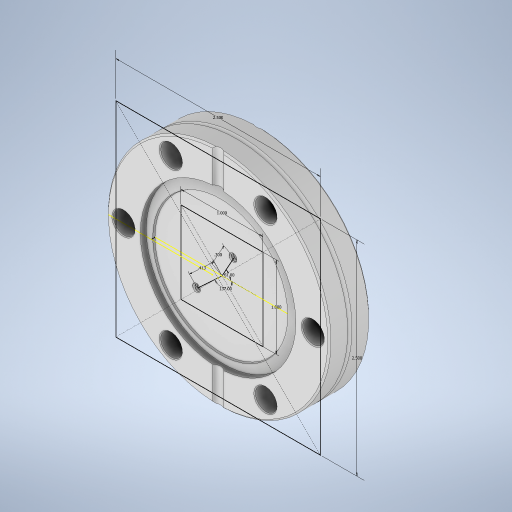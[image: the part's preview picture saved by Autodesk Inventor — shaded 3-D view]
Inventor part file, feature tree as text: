
AUTODESK INVENTOR PART (.ipt)
format: ipt  version: 2024 (Build 280153000, 153)  size: 2,524,672 bytes
history: native  units: in
note: dims shown in document units (in); Inventor stores cm internally (conversion verified against a paired STEP export)
features: move_body x7, sketch x4, other x1, boolean_combine x1, pattern_circular x1
ambient origin geometry x8: Origin, YZ Plane, XZ Plane, XY Plane, X Axis, Y Axis, Z Axis, Center Point
bodies: Solid1 (feature_tree), Solid2 (feature_tree), Solid3 (feature_tree)
feature tree (14):
  move_body  "Move Body1"
  move_body  "Move Body2"
  sketch  "Sketch2"  dims[d6=0.0in d7=0.0in d8=-0.1in d9=1.0in d10=0.0in d11=0.0in]
  sketch  "Sketch3"  dims[d12=-1.0in d13=0.0in d14=0.05in]
  sketch  "Sketch4"  dims[d15=1.0in]
  move_body  "Move Body3"
  move_body  "Move Body4"
  sketch  "Sketch5"  dims[d16=1.0in d17=2.5in d18=2.5in d19=0.0in d20=0.0in d21=0.006in d22=0.0in d23=0.0in d24=0.245in d25=0.3001in d26=0.4192in d27=0.4126in d28=0.9414in d29=0.145in d30=0.262in d31=0.0in d32=0.0in d33=0.0in d34=0.251in d35=-0.302in d36=-0.281in d37=0.0in]
  move_body  "Move Body5"
  other  "CirPattern2:1"
  move_body  "Move Body6"
  move_body  "Move Body7"
  boolean_combine  "Combine1"
  pattern_circular  "CirPattern2"
